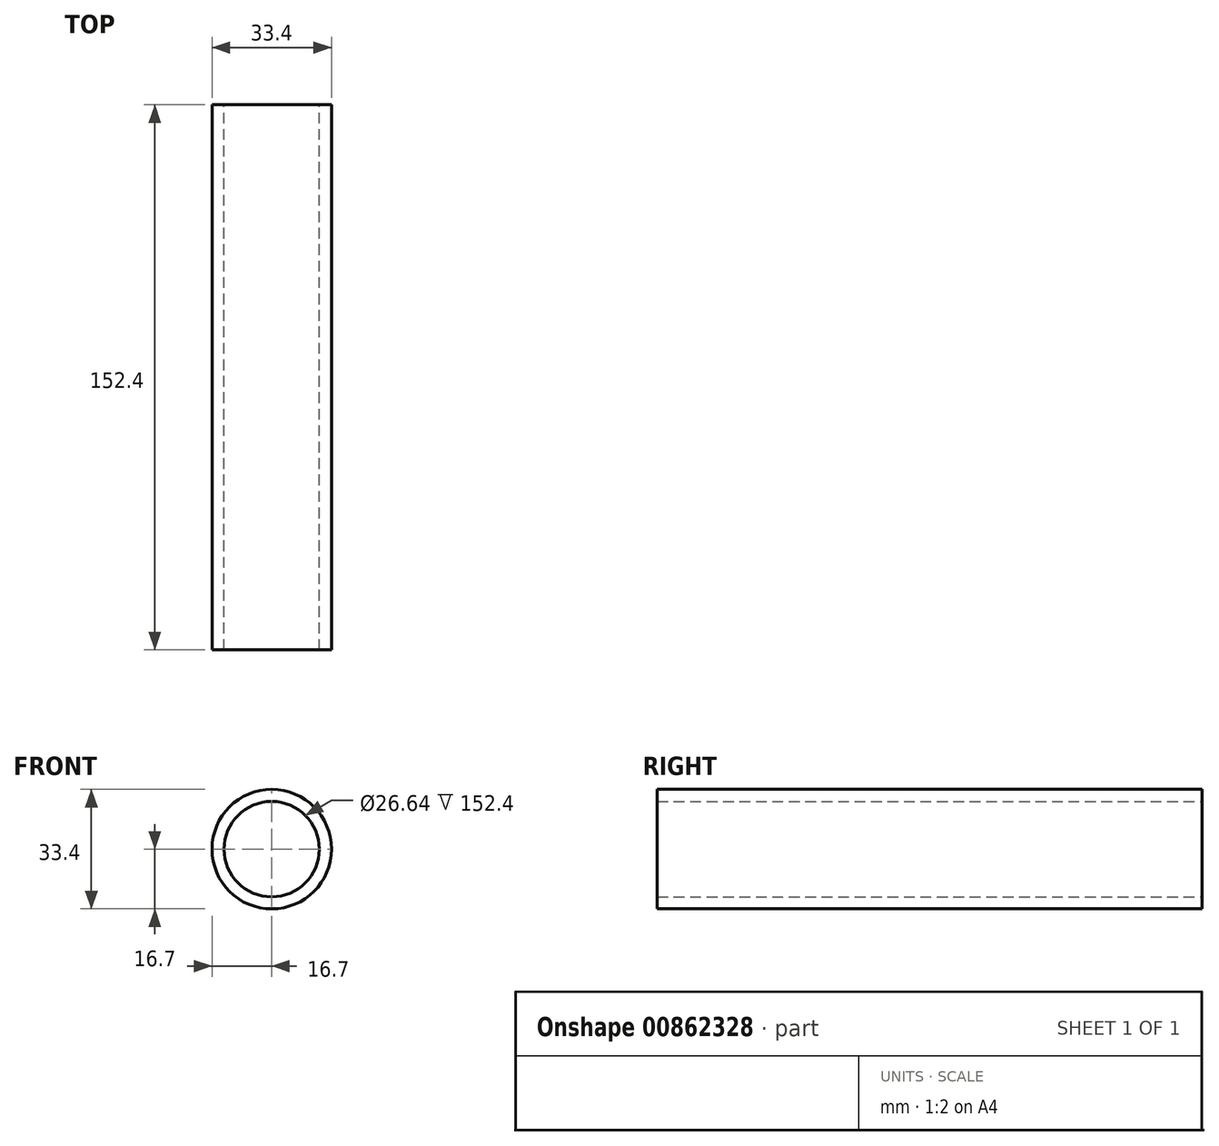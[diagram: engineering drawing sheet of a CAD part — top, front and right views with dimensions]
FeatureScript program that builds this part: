
annotation { "Feature Type Name" : "Feature", "Feature Type Description" : "" }
export const myFeature = defineFeature(function(context is Context, id is Id, definition is map)
    precondition{}
    {
        {
            var Q0;
            Q0=qCreatedBy(makeId("Front.planeOp"),FACE);
            var sketch = newSketch(context, id + "F0", { "sketchPlane" : qUnion([Q0])});
            skCircle(sketch, "E0", {"center": v(0, 0) * mm, "radius": 16.7 * mm});
            skCircle(sketch, "E1", {"center": v(0, 0) * mm, "radius": 13.32 * mm});
            skSolve(sketch);
        }
        {
            var Q0;
            Q0=makeQuery(id+"F0.imprint","IMPRINT",FACE,{"disambiguationData":[TD([[makeQuery(id+"F0.imprint","IMPRINT",EDGE,{"derivedFrom":sQuery(id+"F0.wireOp",EDGE,"E0")}),1.0]])]});
            extrude(context, id + "F1", {"entities" : qUnion([Q0]), "endBound" : BoundingType.SYMMETRIC, "depth" : 152.4 * mm, "offsetDistance" : 25.4 * mm});
        }
    });
